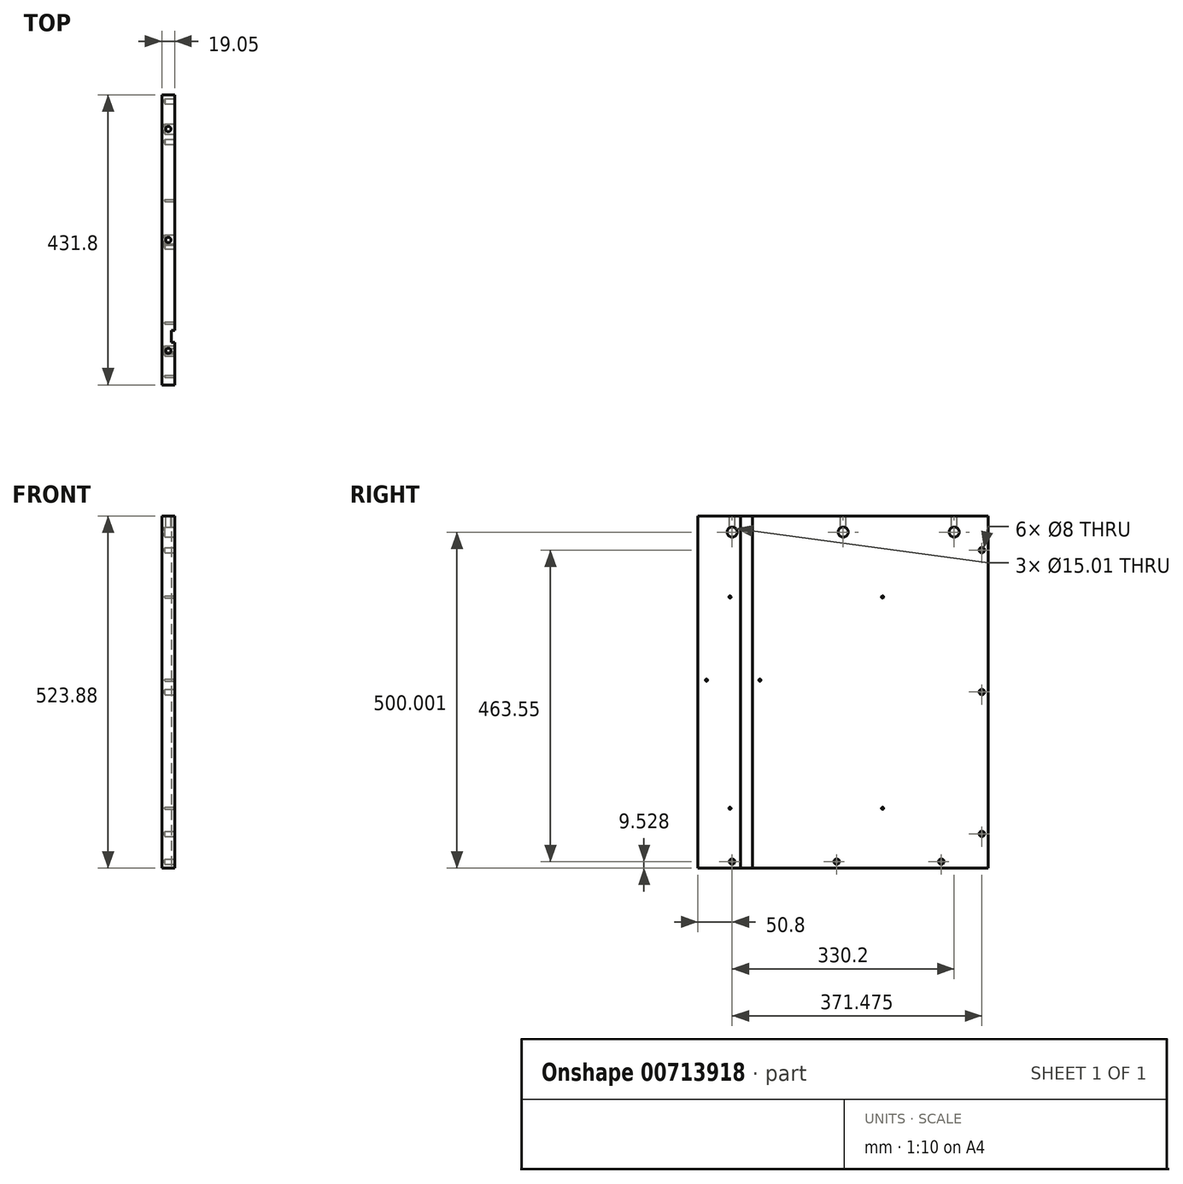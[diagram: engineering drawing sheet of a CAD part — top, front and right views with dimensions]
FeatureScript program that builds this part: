
annotation { "Feature Type Name" : "Feature", "Feature Type Description" : "" }
export const myFeature = defineFeature(function(context is Context, id is Id, definition is map)
    precondition{}
    {
        {
            var Q0;
            Q0=qCreatedBy(makeId("Right.planeOp"),FACE);
            var sketch = newSketch(context, id + "F0", { "sketchPlane" : qUnion([Q0])});
            skLineSegment(sketch, "E0.bottom", {"start": v(215.9, 261.94) * mm, "end": v(-215.9, 261.94) * mm});
            skLineSegment(sketch, "E0.top", {"start": v(215.9, -261.94) * mm, "end": v(-215.9, -261.94) * mm});
            skLineSegment(sketch, "E0.left", {"start": v(215.9, 261.94) * mm, "end": v(215.9, -261.94) * mm});
            skLineSegment(sketch, "E0.right", {"start": v(-215.9, 261.94) * mm, "end": v(-215.9, -261.94) * mm});
            skPoint(sketch, "E0.middle", {"position": v(0, 0) * mm});
            skSolve(sketch);
        }
        {
            var Q0;
            Q0=makeQuery(id+"F0.imprint","IMPRINT",FACE,{"disambiguationData":[TD([[makeQuery(id+"F0.imprint","IMPRINT",EDGE,{"derivedFrom":sQuery(id+"F0.wireOp",EDGE,"E0.bottom")}),1.0]])]});
            extrude(context, id + "F1", {"entities" : qUnion([Q0]), "depth" : 19.05 * mm, "offsetDistance" : 25.4 * mm});
        }
        {
            var Q0;
            Q0=makeQuery(id+"F1.opExtrude","CAP_FACE",FACE,{"disambiguationData":[OSD([sQuery(id+"F0.wireOp",EDGE,"E0.bottom"),sQuery(id+"F0.wireOp",EDGE,"E0.top"),sQuery(id+"F0.wireOp",EDGE,"E0.left"),sQuery(id+"F0.wireOp",EDGE,"E0.right")])],"isStart":false});
            var sketch = newSketch(context, id + "F2", { "sketchPlane" : qUnion([Q0])});
            skLineSegment(sketch, "E1", {"start": v(-215.9, 261.94) * mm, "end": v(-215.9, 238.06) * mm});
            skLineSegment(sketch, "E2", {"start": v(-215.9, 238.06) * mm, "end": v(215.9, 238.06) * mm});
            skLineSegment(sketch, "E3", {"start": v(215.9, 261.94) * mm, "end": v(206.38, 261.94) * mm});
            skLineSegment(sketch, "E4", {"start": v(206.38, 261.94) * mm, "end": v(206.38, -261.94) * mm});
            skLineSegment(sketch, "E5", {"start": v(206.38, -261.94) * mm, "end": v(206.38, -211.14) * mm});
            skLineSegment(sketch, "E6", {"start": v(215.9, 0) * mm, "end": v(206.38, 0) * mm});
            skLineSegment(sketch, "E7", {"start": v(206.38, 261.94) * mm, "end": v(206.38, 211.14) * mm});
            skPoint(sketch, "E8", {"position": v(206.38, 211.14) * mm});
            skPoint(sketch, "E9", {"position": v(206.38, 0) * mm});
            skPoint(sketch, "E10", {"position": v(206.38, -211.14) * mm});
            skLineSegment(sketch, "E11", {"start": v(-215.9, -261.94) * mm, "end": v(-215.9, -252.41) * mm});
            skLineSegment(sketch, "E12", {"start": v(-215.9, -252.41) * mm, "end": v(215.9, -252.41) * mm});
            skLineSegment(sketch, "E13", {"start": v(215.9, -252.41) * mm, "end": v(146.05, -252.41) * mm});
            skLineSegment(sketch, "E14", {"start": v(-215.9, -252.41) * mm, "end": v(-165.1, -252.41) * mm});
            skLineSegment(sketch, "E15", {"start": v(-215.9, -252.41) * mm, "end": v(-9.53, -252.41) * mm});
            skPoint(sketch, "E16", {"position": v(-165.1, -252.41) * mm});
            skPoint(sketch, "E17", {"position": v(-9.53, -252.41) * mm});
            skPoint(sketch, "E18", {"position": v(146.05, -252.41) * mm});
            skLineSegment(sketch, "E19", {"start": v(-215.9, 238.06) * mm, "end": v(-165.1, 238.06) * mm});
            skLineSegment(sketch, "E20", {"start": v(215.9, 238.06) * mm, "end": v(165.1, 238.06) * mm});
            skLineSegment(sketch, "E21", {"start": v(0, 238.06) * mm, "end": v(0, 261.94) * mm});
            skPoint(sketch, "E22", {"position": v(-165.1, 238.06) * mm});
            skPoint(sketch, "E23", {"position": v(0, 238.06) * mm});
            skPoint(sketch, "E24", {"position": v(165.1, 238.06) * mm});
            skSolve(sketch);
        }
        {
            var Q0;
            Q0=sQuery(id+"F2.wireOp",VERTEX,"E8");
            var Q1;
            Q1=sQuery(id+"F2.wireOp",VERTEX,"E10");
            var Q2;
            Q2=sQuery(id+"F2.wireOp",VERTEX,"E18");
            var Q3;
            Q3=sQuery(id+"F2.wireOp",VERTEX,"E17");
            var Q4;
            Q4=sQuery(id+"F2.wireOp",VERTEX,"E16");
            var Q5;
            Q5=sQuery(id+"F2.wireOp",VERTEX,"E9");
            var Q6;
            Q6=makeQuery(id+"F1.opExtrude","SWEPT_BODY",BODY,{"disambiguationData":[OSD([sQuery(id+"F0.wireOp",EDGE,"E0.bottom"),sQuery(id+"F0.wireOp",EDGE,"E0.top"),sQuery(id+"F0.wireOp",EDGE,"E0.left"),sQuery(id+"F0.wireOp",EDGE,"E0.right")])]});
            hole(context, id + "F3", {"style" : HoleStyle.SIMPLE, "endStyle" : HoleEndStyle.BLIND, "holeDiameter" : 8 * mm, "majorDiameter" : 6.35 * mm, "holeDepth" : 14.22 * mm, "isTappedThrough" : true, "tappedDepth" : 12.7 * mm, "tapClearance" : 3, "startFromSketch" : true, "locations" : qUnion([Q0, Q1, Q2, Q3, Q4, Q5]), "scope" : qUnion([Q6])});
        }
        {
            var Q0;
            Q0=sQuery(id+"F2.wireOp",VERTEX,"E22");
            var Q1;
            Q1=sQuery(id+"F2.wireOp",VERTEX,"E23");
            var Q2;
            Q2=sQuery(id+"F2.wireOp",VERTEX,"E24");
            var Q3;
            Q3=makeQuery(id+"F1.opExtrude","SWEPT_BODY",BODY,{"disambiguationData":[OSD([sQuery(id+"F0.wireOp",EDGE,"E0.bottom"),sQuery(id+"F0.wireOp",EDGE,"E0.top"),sQuery(id+"F0.wireOp",EDGE,"E0.left"),sQuery(id+"F0.wireOp",EDGE,"E0.right")])]});
            hole(context, id + "F4", {"style" : HoleStyle.SIMPLE, "endStyle" : HoleEndStyle.BLIND, "holeDiameter" : 15 * mm, "majorDiameter" : 6.35 * mm, "holeDepth" : 14.22 * mm, "isTappedThrough" : true, "tappedDepth" : 12.7 * mm, "tapClearance" : 3, "startFromSketch" : true, "locations" : qUnion([Q0, Q1, Q2]), "scope" : qUnion([Q3])});
        }
        {
            var Q0;
            Q0=makeQuery(id+"F1.opExtrude","SWEPT_FACE",FACE,{"disambiguationData":[OSD([sQuery(id+"F0.wireOp",EDGE,"E0.bottom")])]});
            var sketch = newSketch(context, id + "F5", { "sketchPlane" : qUnion([Q0])});
            skLineSegment(sketch, "E25", {"start": v(9.53, 215.9) * mm, "end": v(9.53, 165.1) * mm});
            skLineSegment(sketch, "E26", {"start": v(9.53, -215.9) * mm, "end": v(9.53, -165.1) * mm});
            skLineSegment(sketch, "E27", {"start": v(19.05, 0) * mm, "end": v(9.52, 0) * mm});
            skPoint(sketch, "E28", {"position": v(9.53, 165.1) * mm});
            skPoint(sketch, "E29", {"position": v(9.52, 0) * mm});
            skPoint(sketch, "E30", {"position": v(9.53, -165.1) * mm});
            skSolve(sketch);
        }
        {
            var Q0;
            Q0=sQuery(id+"F5.wireOp",VERTEX,"E28");
            var Q1;
            Q1=sQuery(id+"F5.wireOp",VERTEX,"E29");
            var Q2;
            Q2=sQuery(id+"F5.wireOp",VERTEX,"E30");
            var Q3;
            Q3=makeQuery(id+"F1.opExtrude","SWEPT_BODY",BODY,{"disambiguationData":[OSD([sQuery(id+"F0.wireOp",EDGE,"E0.bottom"),sQuery(id+"F0.wireOp",EDGE,"E0.top"),sQuery(id+"F0.wireOp",EDGE,"E0.left"),sQuery(id+"F0.wireOp",EDGE,"E0.right")])]});
            hole(context, id + "F6", {"style" : HoleStyle.SIMPLE, "endStyle" : HoleEndStyle.BLIND, "holeDiameter" : 8 * mm, "majorDiameter" : 6.35 * mm, "holeDepth" : 25.4 * mm, "isTappedThrough" : true, "tappedDepth" : 12.7 * mm, "tapClearance" : 3, "startFromSketch" : true, "locations" : qUnion([Q0, Q1, Q2]), "scope" : qUnion([Q3])});
        }
        {
            var Q0;
            Q0=makeQuery(id+"F1.opExtrude","CAP_FACE",FACE,{"disambiguationData":[OSD([sQuery(id+"F0.wireOp",EDGE,"E0.bottom"),sQuery(id+"F0.wireOp",EDGE,"E0.top"),sQuery(id+"F0.wireOp",EDGE,"E0.left"),sQuery(id+"F0.wireOp",EDGE,"E0.right")])],"isStart":false});
            var sketch = newSketch(context, id + "F7", { "sketchPlane" : qUnion([Q0])});
            skLineSegment(sketch, "E31", {"start": v(-215.9, -261.94) * mm, "end": v(-215.9, -173.04) * mm});
            skLineSegment(sketch, "E32", {"start": v(-215.9, -173.04) * mm, "end": v(58.74, -173.04) * mm});
            skLineSegment(sketch, "E33", {"start": v(-215.9, -173.04) * mm, "end": v(-168.28, -173.04) * mm});
            skLineSegment(sketch, "E34", {"start": v(-215.9, -261.94) * mm, "end": v(-215.9, 141.41) * mm});
            skLineSegment(sketch, "E35", {"start": v(-215.9, 141.41) * mm, "end": v(58.74, 141.41) * mm});
            skLineSegment(sketch, "E36", {"start": v(-215.9, 141.41) * mm, "end": v(-168.28, 141.41) * mm});
            skLineSegment(sketch, "E37", {"start": v(-215.9, -261.94) * mm, "end": v(-215.9, 17.72) * mm});
            skLineSegment(sketch, "E38", {"start": v(-215.9, 17.72) * mm, "end": v(-123.82, 17.72) * mm});
            skLineSegment(sketch, "E39", {"start": v(-215.9, 17.72) * mm, "end": v(-203.2, 17.72) * mm});
            skPoint(sketch, "E40", {"position": v(-168.28, 141.41) * mm});
            skPoint(sketch, "E41", {"position": v(58.74, 141.41) * mm});
            skPoint(sketch, "E42", {"position": v(-203.2, 17.72) * mm});
            skPoint(sketch, "E43", {"position": v(-123.82, 17.72) * mm});
            skPoint(sketch, "E44", {"position": v(-168.28, -173.04) * mm});
            skPoint(sketch, "E45", {"position": v(58.74, -173.04) * mm});
            skSolve(sketch);
        }
        {
            var Q0;
            Q0=sQuery(id+"F7.wireOp",VERTEX,"E40");
            var Q1;
            Q1=sQuery(id+"F7.wireOp",VERTEX,"E41");
            var Q2;
            Q2=sQuery(id+"F7.wireOp",VERTEX,"E42");
            var Q3;
            Q3=sQuery(id+"F7.wireOp",VERTEX,"E43");
            var Q4;
            Q4=sQuery(id+"F7.wireOp",VERTEX,"E44");
            var Q5;
            Q5=sQuery(id+"F7.wireOp",VERTEX,"E45");
            var Q6;
            Q6=makeQuery(id+"F1.opExtrude","SWEPT_BODY",BODY,{"disambiguationData":[OSD([sQuery(id+"F0.wireOp",EDGE,"E0.bottom"),sQuery(id+"F0.wireOp",EDGE,"E0.top"),sQuery(id+"F0.wireOp",EDGE,"E0.left"),sQuery(id+"F0.wireOp",EDGE,"E0.right")])]});
            hole(context, id + "F8", {"style" : HoleStyle.SIMPLE, "endStyle" : HoleEndStyle.BLIND, "holeDiameter" : 3.17 * mm, "majorDiameter" : 6.35 * mm, "holeDepth" : 14.22 * mm, "isTappedThrough" : true, "tappedDepth" : 12.7 * mm, "tapClearance" : 3, "startFromSketch" : true, "locations" : qUnion([Q0, Q1, Q2, Q3, Q4, Q5]), "scope" : qUnion([Q6])});
        }
        {
            var Q0;
            Q0=makeQuery(id+"F1.opExtrude","CAP_FACE",FACE,{"disambiguationData":[OSD([sQuery(id+"F0.wireOp",EDGE,"E0.bottom"),sQuery(id+"F0.wireOp",EDGE,"E0.top"),sQuery(id+"F0.wireOp",EDGE,"E0.left"),sQuery(id+"F0.wireOp",EDGE,"E0.right")])],"isStart":false});
            var sketch = newSketch(context, id + "F9", { "sketchPlane" : qUnion([Q0])});
            skLineSegment(sketch, "E46", {"start": v(-215.9, 261.94) * mm, "end": v(-152.4, 261.94) * mm});
            skLineSegment(sketch, "E47.bottom", {"start": v(-152.4, 261.94) * mm, "end": v(-134.87, 261.94) * mm});
            skLineSegment(sketch, "E47.top", {"start": v(-152.4, -261.94) * mm, "end": v(-134.87, -261.94) * mm});
            skLineSegment(sketch, "E47.left", {"start": v(-152.4, 261.94) * mm, "end": v(-152.4, -261.94) * mm});
            skLineSegment(sketch, "E47.right", {"start": v(-134.87, 261.94) * mm, "end": v(-134.87, -261.94) * mm});
            skSolve(sketch);
        }
        {
            var Q0;
            Q0=makeQuery(id+"F9.imprint","IMPRINT",FACE,{"disambiguationData":[TD([[makeQuery(id+"F9.imprint","IMPRINT",EDGE,{"derivedFrom":sQuery(id+"F9.wireOp",EDGE,"E47.bottom")}),1.0]])]});
            extrude(context, id + "F10", {"entities" : qUnion([Q0]), "operationType" : NewBodyOperationType.REMOVE, "oppositeDirection" : true, "depth" : 4.83 * mm, "offsetDistance" : 25.4 * mm});
        }
    });
